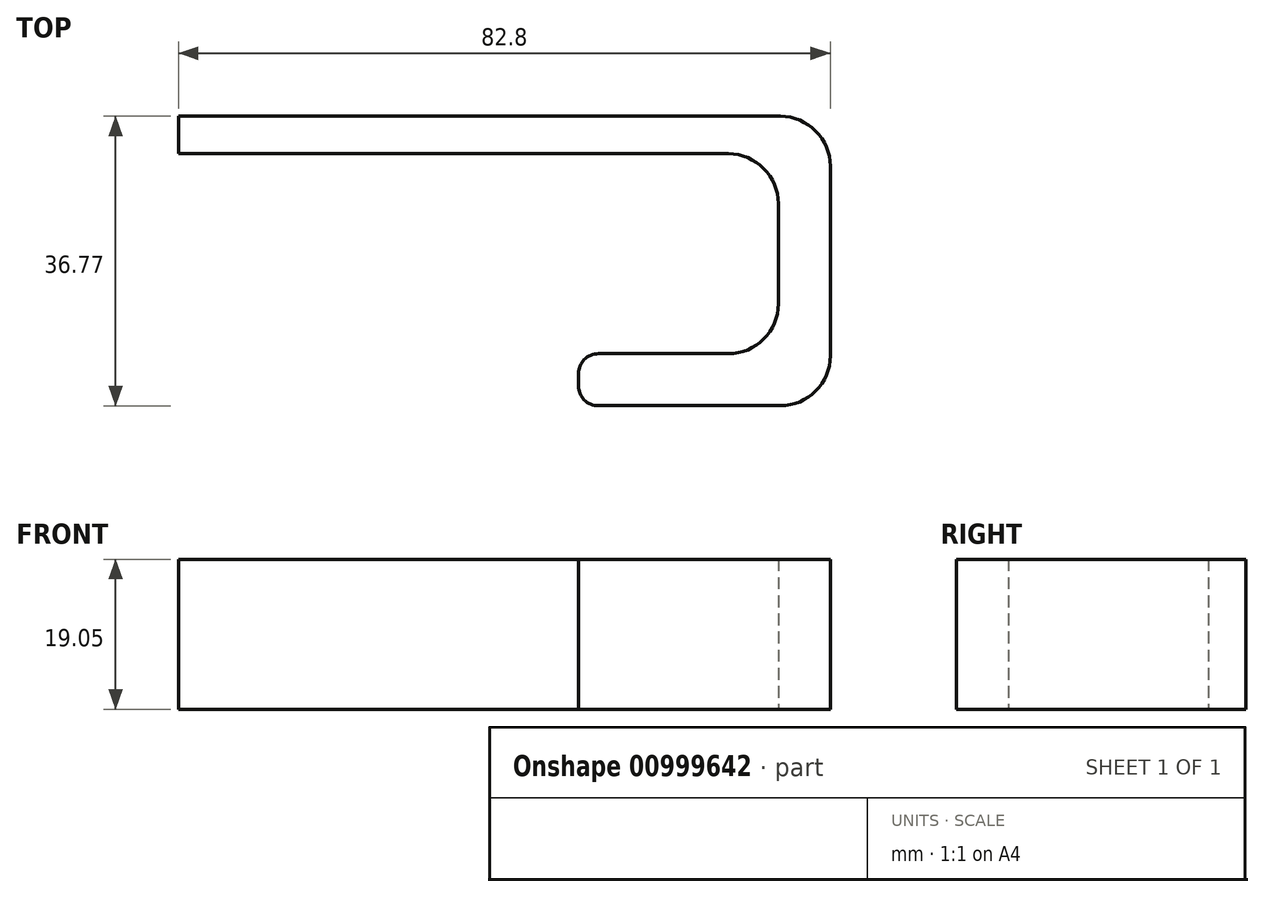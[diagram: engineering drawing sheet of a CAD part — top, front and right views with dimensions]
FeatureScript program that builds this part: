
annotation { "Feature Type Name" : "Feature", "Feature Type Description" : "" }
export const myFeature = defineFeature(function(context is Context, id is Id, definition is map)
    precondition{}
    {
        {
            var Q0;
            Q0=qCreatedBy(makeId("Top.planeOp"),FACE);
            var sketch = newSketch(context, id + "F0", { "sketchPlane" : qUnion([Q0])});
            skLineSegment(sketch, "E0.bottom", {"start": v(0, 0) * mm, "end": v(76.45, 0) * mm});
            skLineSegment(sketch, "E0.top", {"start": v(0, -4.76) * mm, "end": v(69.85, -4.76) * mm});
            skLineSegment(sketch, "E0.left", {"start": v(0, 0) * mm, "end": v(0, -4.76) * mm});
            skLineSegment(sketch, "E1", {"start": v(76.2, -11.11) * mm, "end": v(76.2, -23.81) * mm});
            skLineSegment(sketch, "E2", {"start": v(69.85, -30.16) * mm, "end": v(53.34, -30.16) * mm});
            skLineSegment(sketch, "E3.0", {"start": v(76.45, -36.77) * mm, "end": v(53.34, -36.77) * mm});
            skLineSegment(sketch, "E3.1", {"start": v(82.8, -6.35) * mm, "end": v(82.8, -30.42) * mm});
            skLineSegment(sketch, "E4", {"start": v(50.8, -32.7) * mm, "end": v(50.8, -34.23) * mm});
            skPoint(sketch, "E5.visualSharp", {"position": v(76.2, -4.76) * mm});
            skArc(sketch, "E5.filletArc", {"start": v(76.2, -11.11) * mm, "mid": v(74.34, -6.62) * mm, "end": v(69.85, -4.76) * mm});
            skPoint(sketch, "E6.visualSharp", {"position": v(76.2, -30.16) * mm});
            skArc(sketch, "E6.filletArc", {"start": v(69.85, -30.16) * mm, "mid": v(74.34, -28.3) * mm, "end": v(76.2, -23.81) * mm});
            skPoint(sketch, "E7.visualSharp", {"position": v(82.8, 0) * mm});
            skArc(sketch, "E7.filletArc", {"start": v(82.8, -6.35) * mm, "mid": v(80.94, -1.86) * mm, "end": v(76.45, 0) * mm});
            skPoint(sketch, "E8.visualSharp", {"position": v(82.8, -36.77) * mm});
            skArc(sketch, "E8.filletArc", {"start": v(76.45, -36.77) * mm, "mid": v(80.94, -34.9) * mm, "end": v(82.8, -30.42) * mm});
            skPoint(sketch, "E9.visualSharp", {"position": v(50.8, -30.16) * mm});
            skArc(sketch, "E9.filletArc", {"start": v(53.34, -30.16) * mm, "mid": v(51.54, -30.9) * mm, "end": v(50.8, -32.7) * mm});
            skPoint(sketch, "E10.visualSharp", {"position": v(50.8, -36.77) * mm});
            skArc(sketch, "E10.filletArc", {"start": v(50.8, -34.23) * mm, "mid": v(51.54, -36.02) * mm, "end": v(53.34, -36.77) * mm});
            skSolve(sketch);
        }
        {
            var Q0;
            Q0=makeQuery(id+"F0.imprint","IMPRINT",FACE,{"disambiguationData":[TD([[makeQuery(id+"F0.imprint","IMPRINT",EDGE,{"derivedFrom":sQuery(id+"F0.wireOp",EDGE,"E0.bottom")}),-1.0]])]});
            extrude(context, id + "F1", {"entities" : qUnion([Q0]), "depth" : 19.05 * mm, "offsetDistance" : 25.4 * mm});
        }
    });
